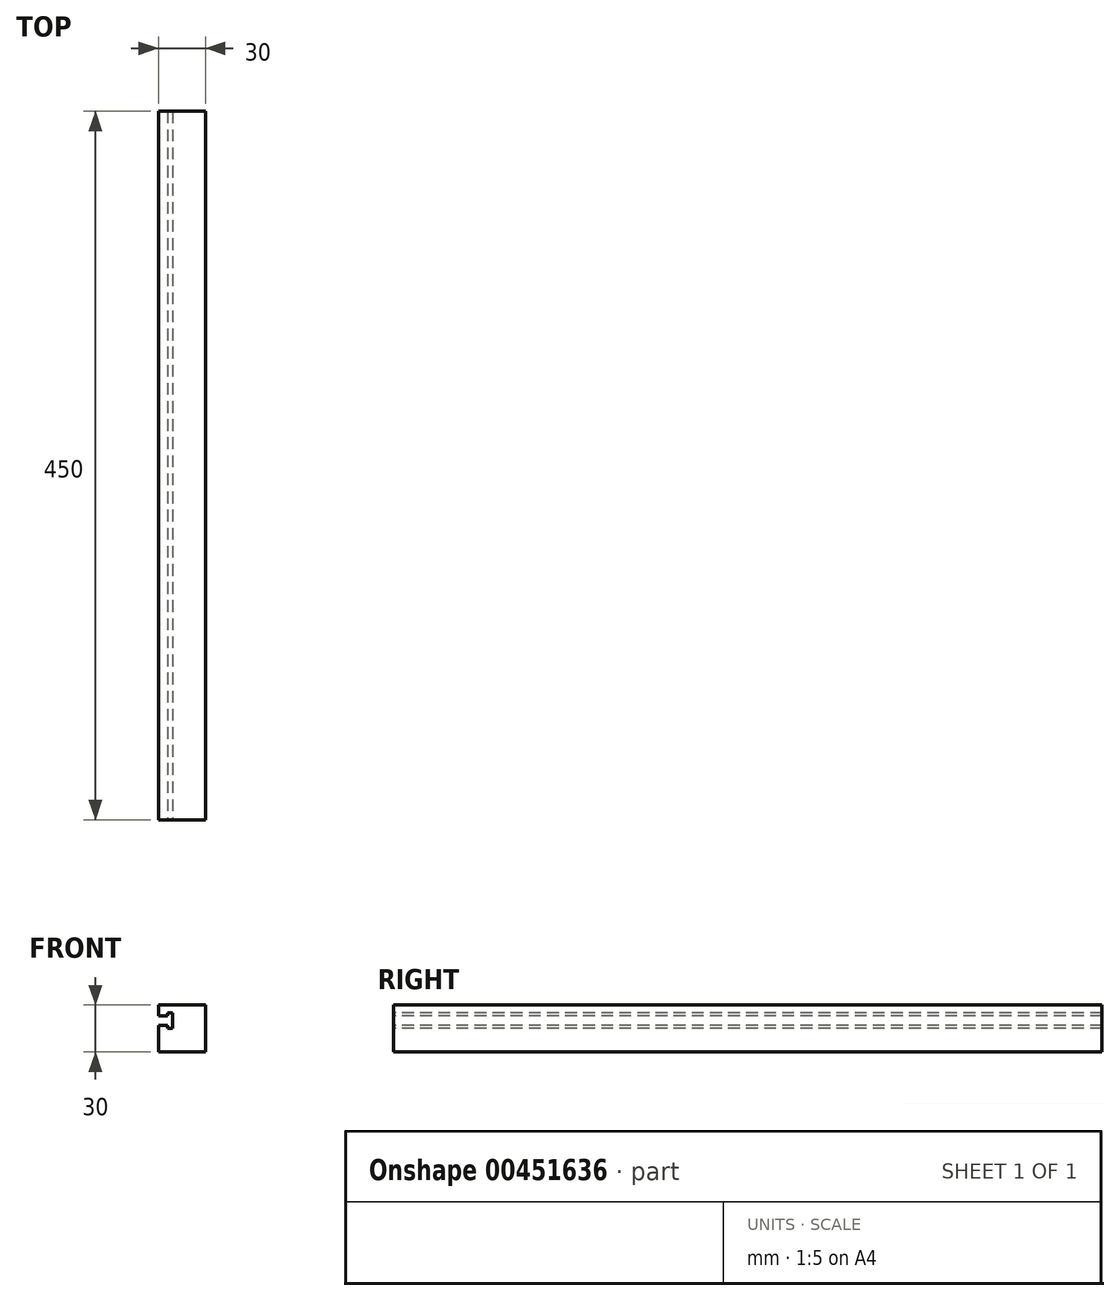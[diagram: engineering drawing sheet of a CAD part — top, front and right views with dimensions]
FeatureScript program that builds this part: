
annotation { "Feature Type Name" : "Feature", "Feature Type Description" : "" }
export const myFeature = defineFeature(function(context is Context, id is Id, definition is map)
    precondition{}
    {
        {
            var Q0;
            Q0=qCreatedBy(makeId("Front.planeOp"),FACE);
            var sketch = newSketch(context, id + "F0", { "sketchPlane" : qUnion([Q0])});
            skLineSegment(sketch, "E0.bottom", {"start": v(15, 15) * mm, "end": v(-15, 15) * mm});
            skLineSegment(sketch, "E0.top", {"start": v(15, -15) * mm, "end": v(-15, -15) * mm});
            skLineSegment(sketch, "E0.left", {"start": v(15, 15) * mm, "end": v(15, -15) * mm});
            skLineSegment(sketch, "E0.right", {"start": v(-15, 15) * mm, "end": v(-15, -15) * mm});
            skPoint(sketch, "E0.middle", {"position": v(0, 0) * mm});
            skSolve(sketch);
        }
        {
            var Q0;
            Q0 = qSketchRegion(id + "F0", true);
            extrude(context, id + "F1", {"entities" : qUnion([Q0]), "depth" : 225 * mm, "hasSecondDirection" : true, "secondDirectionOppositeDirection" : true, "secondDirectionDepth" : 225 * mm});
        }
        {
            var Q0;
            Q0=makeQuery(id+"F1.opExtrude","CAP_FACE",FACE,{"disambiguationData":[OSD([sQuery(id+"F0.wireOp",EDGE,"E0.bottom"),sQuery(id+"F0.wireOp",EDGE,"E0.top"),sQuery(id+"F0.wireOp",EDGE,"E0.left"),sQuery(id+"F0.wireOp",EDGE,"E0.right")])],"isStart":false});
            var sketch = newSketch(context, id + "F2", { "sketchPlane" : qUnion([Q0])});
            skLineSegment(sketch, "E1", {"start": v(-15, 8) * mm, "end": v(-9, 8) * mm});
            skLineSegment(sketch, "E2", {"start": v(-9, 8) * mm, "end": v(-9, 10) * mm});
            skLineSegment(sketch, "E3", {"start": v(-9, 10) * mm, "end": v(-6, 10) * mm});
            skLineSegment(sketch, "E4", {"start": v(-6, 10) * mm, "end": v(-6, 0) * mm});
            skLineSegment(sketch, "E5", {"start": v(-6, 0) * mm, "end": v(-9, 0) * mm});
            skLineSegment(sketch, "E6", {"start": v(-9, 0) * mm, "end": v(-9, 2) * mm});
            skLineSegment(sketch, "E7", {"start": v(-9, 2) * mm, "end": v(-15, 2) * mm});
            skLineSegment(sketch, "E8", {"start": v(-15, 2) * mm, "end": v(-15, 8) * mm});
            skSolve(sketch);
        }
        {
            var Q0;
            Q0 = qSketchRegion(id + "F2", true);
            extrude(context, id + "F3", {"entities" : qUnion([Q0]), "operationType" : NewBodyOperationType.REMOVE, "endBound" : BoundingType.THROUGH_ALL, "oppositeDirection" : true, "depth" : 25 * mm});
        }
    });
